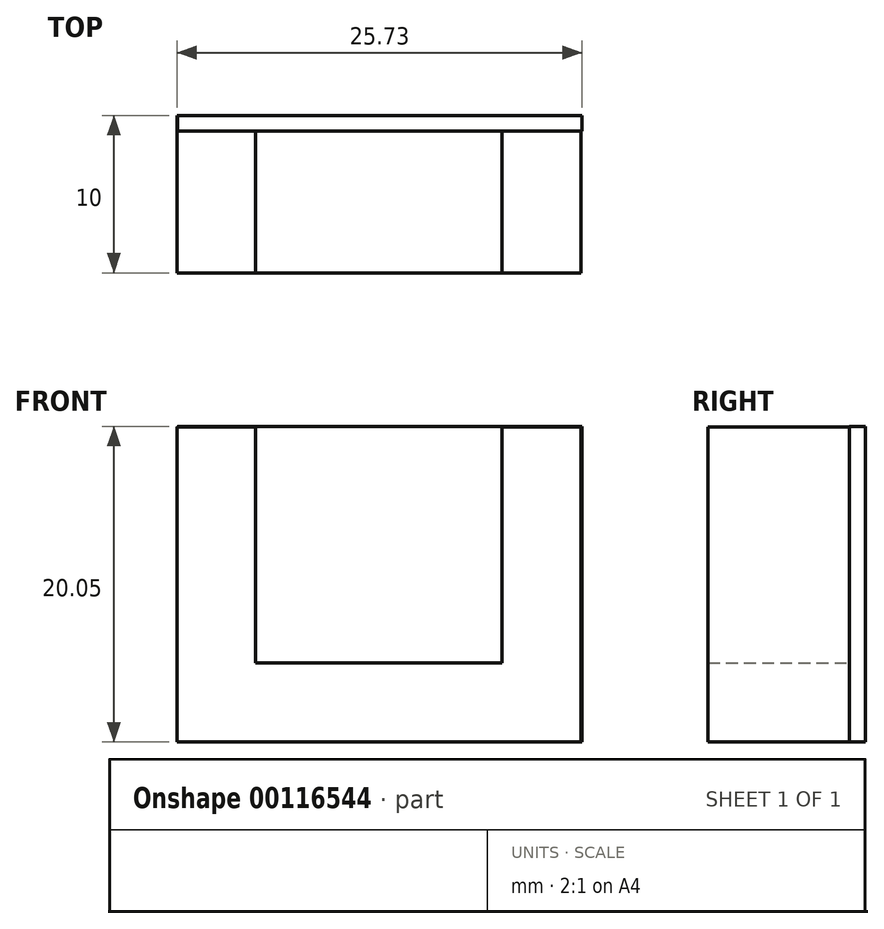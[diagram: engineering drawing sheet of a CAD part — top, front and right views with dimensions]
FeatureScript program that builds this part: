
annotation { "Feature Type Name" : "Feature", "Feature Type Description" : "" }
export const myFeature = defineFeature(function(context is Context, id is Id, definition is map)
    precondition{}
    {
        {
            var Q0;
            Q0=qCreatedBy(makeId("Front.planeOp"),FACE);
            var sketch = newSketch(context, id + "F0", { "sketchPlane" : qUnion([Q0])});
            skLineSegment(sketch, "E0.bottom", {"start": v(-34.19, 35.45) * mm, "end": v(-29.19, 35.45) * mm});
            skLineSegment(sketch, "E0.top", {"start": v(-34.19, 15.45) * mm, "end": v(-29.19, 15.45) * mm});
            skLineSegment(sketch, "E0.left", {"start": v(-34.19, 35.45) * mm, "end": v(-34.19, 15.45) * mm});
            skLineSegment(sketch, "E0.right", {"start": v(-29.19, 35.45) * mm, "end": v(-29.19, 15.45) * mm});
            skLineSegment(sketch, "E1.bottom", {"start": v(-29.19, 15.45) * mm, "end": v(-13.52, 15.45) * mm});
            skLineSegment(sketch, "E1.top", {"start": v(-29.19, 20.45) * mm, "end": v(-13.52, 20.45) * mm});
            skLineSegment(sketch, "E1.left", {"start": v(-29.19, 15.45) * mm, "end": v(-29.19, 20.45) * mm});
            skLineSegment(sketch, "E1.right", {"start": v(-13.52, 15.45) * mm, "end": v(-13.52, 20.45) * mm});
            skLineSegment(sketch, "E2.bottom", {"start": v(-13.52, 15.45) * mm, "end": v(-8.52, 15.45) * mm});
            skLineSegment(sketch, "E2.top", {"start": v(-13.52, 35.45) * mm, "end": v(-8.52, 35.45) * mm});
            skLineSegment(sketch, "E2.left", {"start": v(-13.52, 15.45) * mm, "end": v(-13.52, 35.45) * mm});
            skLineSegment(sketch, "E2.right", {"start": v(-8.52, 15.45) * mm, "end": v(-8.52, 35.45) * mm});
            skLineSegment(sketch, "E3.bottom", {"start": v(23.6, 35.96) * mm, "end": v(49.27, 35.96) * mm});
            skLineSegment(sketch, "E3.top", {"start": v(23.6, 15.96) * mm, "end": v(49.27, 15.96) * mm});
            skLineSegment(sketch, "E3.left", {"start": v(23.6, 35.96) * mm, "end": v(23.6, 15.96) * mm});
            skLineSegment(sketch, "E3.right", {"start": v(49.27, 35.96) * mm, "end": v(49.27, 15.96) * mm});
            skSolve(sketch);
        }
        {
            var Q0;
            Q0=makeQuery(id+"F0.imprint","IMPRINT",FACE,{"disambiguationData":[TD([[makeQuery(id+"F0.imprint","IMPRINT",EDGE,{"derivedFrom":sQuery(id+"F0.wireOp",EDGE,"E0.bottom")}),-1.0]])]});
            var Q1;
            {var subQ0=sQuery(id+"F0.wireOp",EDGE,"E1.bottom");Q1=makeQuery(id+"F0.imprint","IMPRINT",FACE,{"disambiguationData":[TD([[makeQuery(id+"F0.imprint","IMPRINT",EDGE,{"derivedFrom":subQ0}),1.0]])]});}
            var Q2;
            {var subQ3=sQuery(id+"F0.wireOp",EDGE,"E2.bottom");Q2=makeQuery(id+"F0.imprint","IMPRINT",FACE,{"disambiguationData":[TD([[makeQuery(id+"F0.imprint","IMPRINT",EDGE,{"derivedFrom":subQ3}),1.0]])]});}
            extrude(context, id + "F1", {"entities" : qUnion([Q0, Q1, Q2]), "depth" : 10 * mm});
        }
        {
            var Q0;
            Q0=qCreatedBy(makeId("Front.planeOp"),FACE);
            var sketch = newSketch(context, id + "F2", { "sketchPlane" : qUnion([Q0])});
            skLineSegment(sketch, "E4.bottom", {"start": v(-34.14, 35.48) * mm, "end": v(-8.46, 35.48) * mm});
            skLineSegment(sketch, "E4.top", {"start": v(-34.14, 15.43) * mm, "end": v(-8.46, 15.43) * mm});
            skLineSegment(sketch, "E4.left", {"start": v(-34.14, 35.48) * mm, "end": v(-34.14, 15.43) * mm});
            skLineSegment(sketch, "E4.right", {"start": v(-8.46, 35.48) * mm, "end": v(-8.46, 15.43) * mm});
            skSolve(sketch);
        }
        {
            var Q0;
            Q0 = qSketchRegion(id + "F2", true);
            extrude(context, id + "F3", {"entities" : qUnion([Q0]), "operationType" : NewBodyOperationType.ADD, "depth" : 1 * mm});
        }
    });
